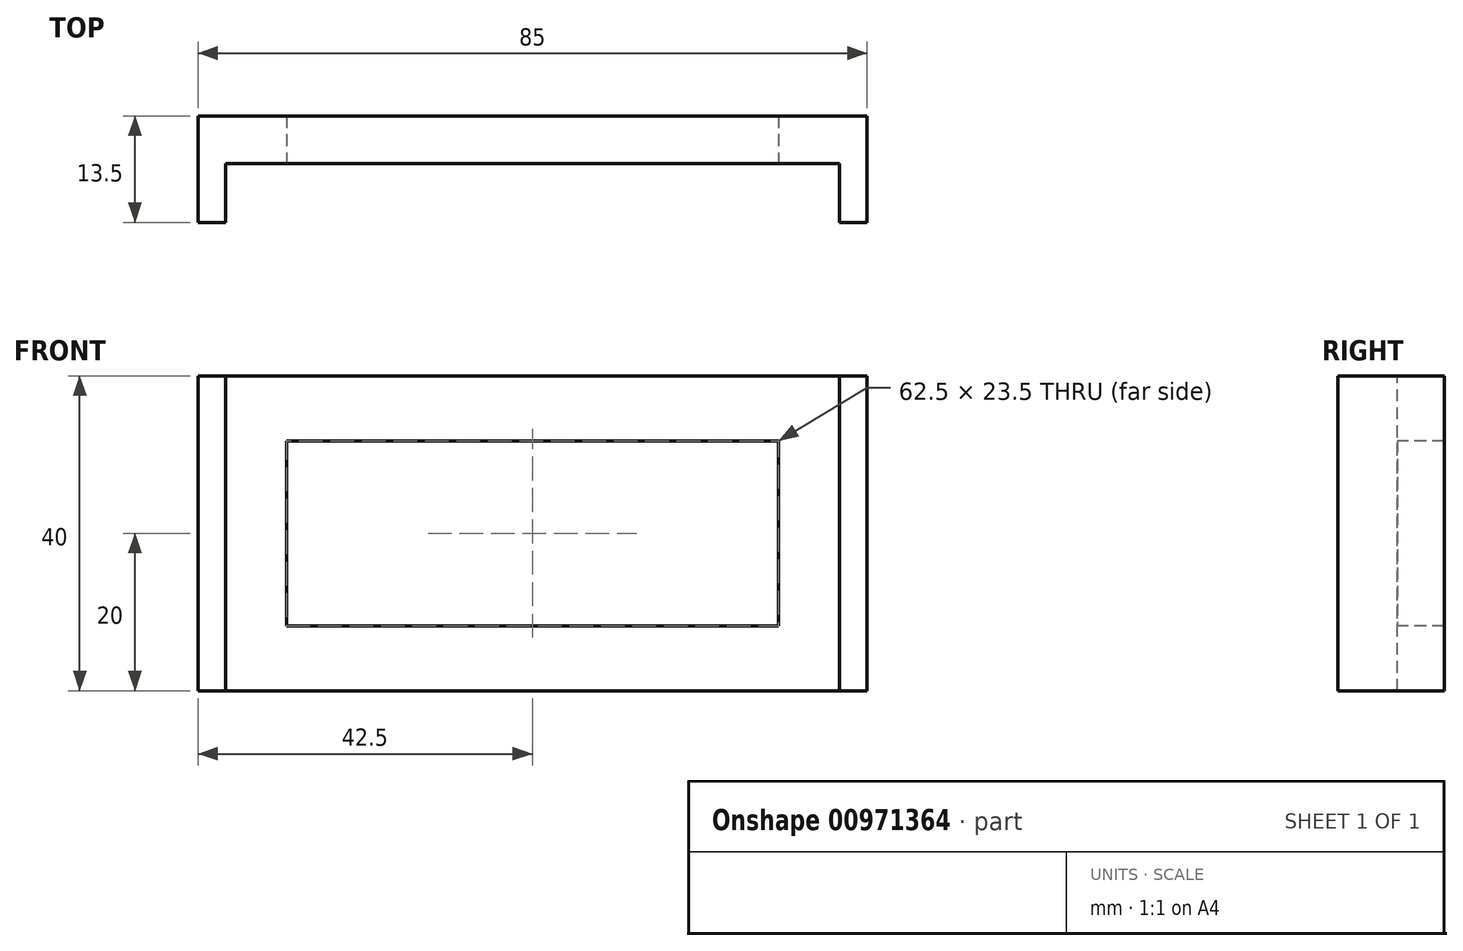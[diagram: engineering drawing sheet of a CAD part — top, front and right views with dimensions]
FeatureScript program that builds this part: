
annotation { "Feature Type Name" : "Feature", "Feature Type Description" : "" }
export const myFeature = defineFeature(function(context is Context, id is Id, definition is map)
    precondition{}
    {
        {
            var Q0;
            Q0=qCreatedBy(makeId("Front.planeOp"),FACE);
            var sketch = newSketch(context, id + "F0", { "sketchPlane" : qUnion([Q0])});
            skLineSegment(sketch, "E0.bottom", {"start": v(-42.5, 20) * mm, "end": v(42.5, 20) * mm});
            skLineSegment(sketch, "E0.top", {"start": v(-42.5, -20) * mm, "end": v(42.5, -20) * mm});
            skLineSegment(sketch, "E0.left", {"start": v(-42.5, 20) * mm, "end": v(-42.5, -20) * mm});
            skLineSegment(sketch, "E0.right", {"start": v(42.5, 20) * mm, "end": v(42.5, -20) * mm});
            skSolve(sketch);
        }
        {
            var Q0;
            Q0 = qSketchRegion(id + "F0", true);
            extrude(context, id + "F1", {"entities" : qUnion([Q0]), "depth" : 6 * mm, "offsetDistance" : 25 * mm});
        }
        {
            var Q0;
            Q0=makeQuery(id+"F1.opExtrude","CAP_FACE",FACE,{"disambiguationData":[OSD([sQuery(id+"F0.wireOp",EDGE,"E0.bottom"),sQuery(id+"F0.wireOp",EDGE,"E0.top"),sQuery(id+"F0.wireOp",EDGE,"E0.left"),sQuery(id+"F0.wireOp",EDGE,"E0.right")])],"isStart":false});
            var sketch = newSketch(context, id + "F2", { "sketchPlane" : qUnion([Q0])});
            skLineSegment(sketch, "E1.bottom", {"start": v(-31.25, 11.75) * mm, "end": v(31.25, 11.75) * mm});
            skLineSegment(sketch, "E1.top", {"start": v(-31.25, -11.75) * mm, "end": v(31.25, -11.75) * mm});
            skLineSegment(sketch, "E1.left", {"start": v(-31.25, 11.75) * mm, "end": v(-31.25, -11.75) * mm});
            skLineSegment(sketch, "E1.right", {"start": v(31.25, 11.75) * mm, "end": v(31.25, -11.75) * mm});
            skSolve(sketch);
        }
        {
            var Q0;
            Q0 = qSketchRegion(id + "F2", true);
            extrude(context, id + "F3", {"entities" : qUnion([Q0]), "operationType" : NewBodyOperationType.REMOVE, "oppositeDirection" : true, "depth" : 25 * mm, "offsetDistance" : 25 * mm});
        }
        {
            var Q0;
            Q0=makeQuery(id+"F1.opExtrude","CAP_FACE",FACE,{"disambiguationData":[OSD([sQuery(id+"F0.wireOp",EDGE,"E0.bottom"),sQuery(id+"F0.wireOp",EDGE,"E0.top"),sQuery(id+"F0.wireOp",EDGE,"E0.left"),sQuery(id+"F0.wireOp",EDGE,"E0.right")])],"isStart":false});
            var sketch = newSketch(context, id + "F4", { "sketchPlane" : qUnion([Q0])});
            skLineSegment(sketch, "E2.bottom", {"start": v(42.5, 20) * mm, "end": v(39, 20) * mm});
            skLineSegment(sketch, "E2.top", {"start": v(42.5, -20) * mm, "end": v(39, -20) * mm});
            skLineSegment(sketch, "E2.left", {"start": v(42.5, 20) * mm, "end": v(42.5, -20) * mm});
            skLineSegment(sketch, "E2.right", {"start": v(39, 20) * mm, "end": v(39, -20) * mm});
            skLineSegment(sketch, "E3.bottom", {"start": v(-42.5, -20) * mm, "end": v(-39, -20) * mm});
            skLineSegment(sketch, "E3.top", {"start": v(-42.5, 20) * mm, "end": v(-39, 20) * mm});
            skLineSegment(sketch, "E3.left", {"start": v(-42.5, -20) * mm, "end": v(-42.5, 20) * mm});
            skLineSegment(sketch, "E3.right", {"start": v(-39, -20) * mm, "end": v(-39, 20) * mm});
            skSolve(sketch);
        }
        {
            var Q0;
            Q0 = qSketchRegion(id + "F4", true);
            extrude(context, id + "F5", {"entities" : qUnion([Q0]), "operationType" : NewBodyOperationType.ADD, "depth" : 7.5 * mm, "offsetDistance" : 25 * mm});
        }
    });
